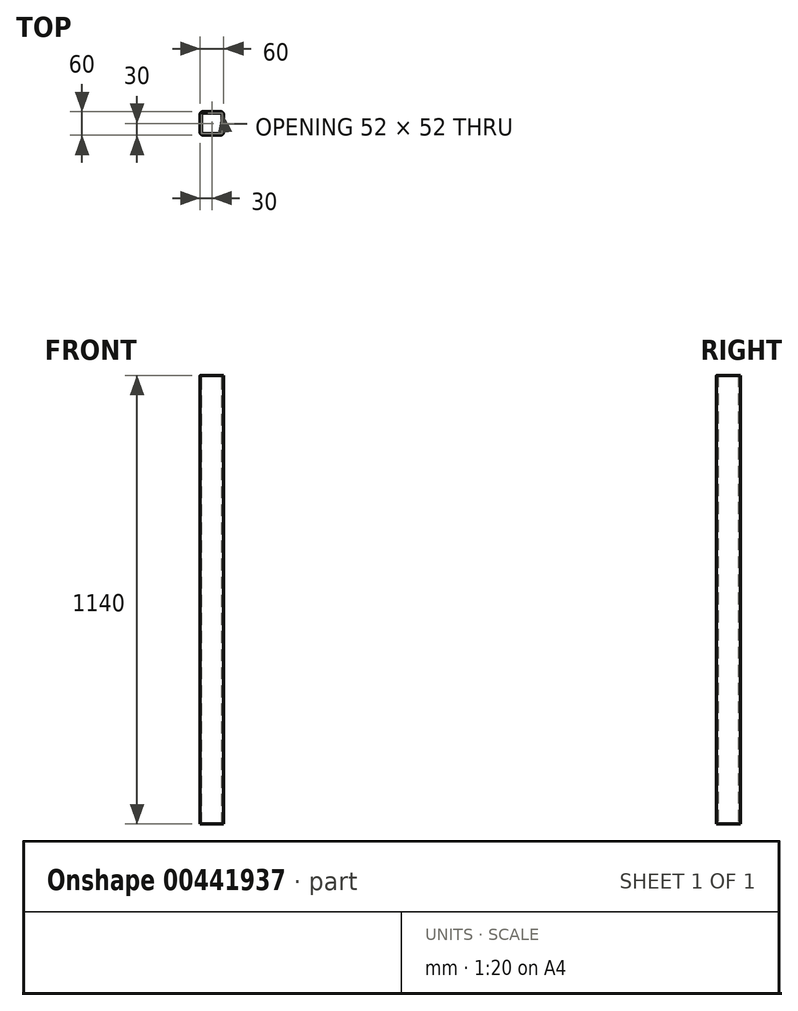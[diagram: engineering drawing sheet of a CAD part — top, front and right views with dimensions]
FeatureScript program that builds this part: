
annotation { "Feature Type Name" : "Feature", "Feature Type Description" : "" }
export const myFeature = defineFeature(function(context is Context, id is Id, definition is map)
    precondition{}
    {
        {
            var Q0;
            Q0=qCreatedBy(makeId("Top.planeOp"),FACE);
            var sketch = newSketch(context, id + "F0", { "sketchPlane" : qUnion([Q0])});
            skLineSegment(sketch, "E0.bottom", {"start": v(30, -30) * mm, "end": v(-30, -30) * mm});
            skLineSegment(sketch, "E0.top", {"start": v(30, 30) * mm, "end": v(-30, 30) * mm});
            skLineSegment(sketch, "E0.left", {"start": v(30, -30) * mm, "end": v(30, 30) * mm});
            skLineSegment(sketch, "E0.right", {"start": v(-30, -30) * mm, "end": v(-30, 30) * mm});
            skPoint(sketch, "E0.middle", {"position": v(0, 0) * mm});
            skSolve(sketch);
        }
        {
            var Q0;
            Q0=makeQuery(id+"F0.imprint","IMPRINT",FACE,{"disambiguationData":[TD([[makeQuery(id+"F0.imprint","IMPRINT",EDGE,{"derivedFrom":sQuery(id+"F0.wireOp",EDGE,"E0.bottom")}),-1.0]])]});
            extrude(context, id + "F1", {"entities" : qUnion([Q0]), "depth" : 1140 * mm});
        }
        {
            var Q0;
            Q0=makeQuery(id+"F1.opExtrude","SWEPT_EDGE",EDGE,{"disambiguationData":[OSD([sQuery(id+"F0.wireOp",EDGE,"E0.bottom"),sQuery(id+"F0.wireOp",EDGE,"E0.right")])]});
            var Q1;
            Q1=makeQuery(id+"F1.opExtrude","SWEPT_EDGE",EDGE,{"disambiguationData":[OSD([sQuery(id+"F0.wireOp",EDGE,"E0.top"),sQuery(id+"F0.wireOp",EDGE,"E0.right")])]});
            var Q2;
            Q2=makeQuery(id+"F1.opExtrude","SWEPT_EDGE",EDGE,{"disambiguationData":[OSD([sQuery(id+"F0.wireOp",EDGE,"E0.bottom"),sQuery(id+"F0.wireOp",EDGE,"E0.left")])]});
            var Q3;
            Q3=makeQuery(id+"F1.opExtrude","SWEPT_EDGE",EDGE,{"disambiguationData":[OSD([sQuery(id+"F0.wireOp",EDGE,"E0.top"),sQuery(id+"F0.wireOp",EDGE,"E0.left")])]});
            fillet(context, id + "F2", {"entities" : qUnion([Q0, Q1, Q2, Q3]), "radius" : 8 * mm, "tangentPropagation" : true, "allowEdgeOverflow" : false});
        }
        {
            var Q0;
            Q0=makeQuery(id+"F1.opExtrude","CAP_FACE",FACE,{"disambiguationData":[OSD([sQuery(id+"F0.wireOp",EDGE,"E0.bottom"),sQuery(id+"F0.wireOp",EDGE,"E0.top"),sQuery(id+"F0.wireOp",EDGE,"E0.left"),sQuery(id+"F0.wireOp",EDGE,"E0.right")])],"isStart":false});
            var Q1;
            Q1=makeQuery(id+"F1.opExtrude","CAP_FACE",FACE,{"disambiguationData":[OSD([sQuery(id+"F0.wireOp",EDGE,"E0.bottom"),sQuery(id+"F0.wireOp",EDGE,"E0.top"),sQuery(id+"F0.wireOp",EDGE,"E0.left"),sQuery(id+"F0.wireOp",EDGE,"E0.right")])],"isStart":true});
            shell(context, id + "F3", {"entities" : qUnion([Q0, Q1]), "thickness" : 4 * mm});
        }
    });
